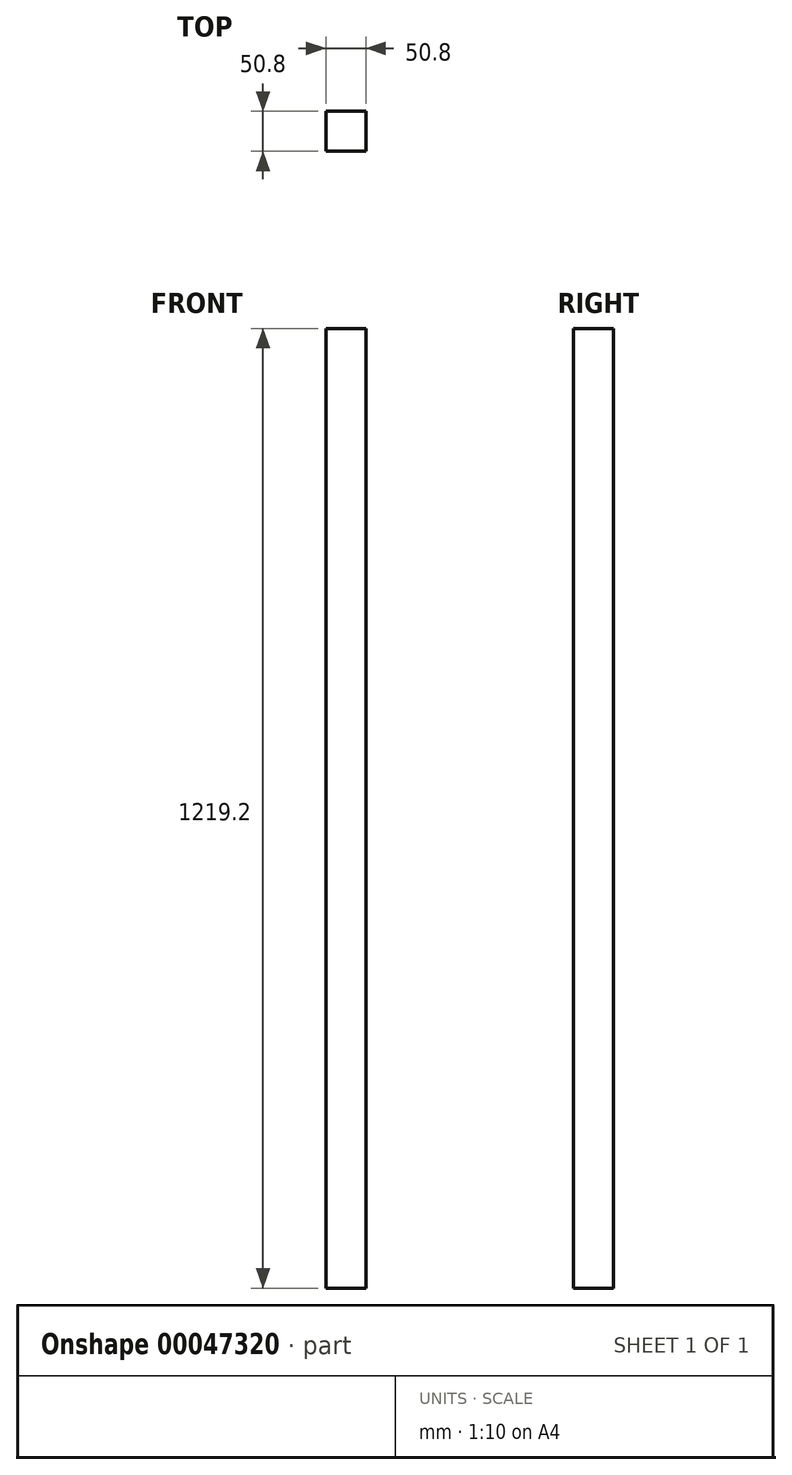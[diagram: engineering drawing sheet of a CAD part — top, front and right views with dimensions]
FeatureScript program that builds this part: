
annotation { "Feature Type Name" : "Feature", "Feature Type Description" : "" }
export const myFeature = defineFeature(function(context is Context, id is Id, definition is map)
    precondition{}
    {
        {
            var Q0;
            Q0=qCreatedBy(makeId("Top.planeOp"),FACE);
            var sketch = newSketch(context, id + "F0", { "sketchPlane" : qUnion([Q0])});
            skLineSegment(sketch, "E0.bottom", {"start": v(-76.33, 69.74) * mm, "end": v(-25.53, 69.74) * mm});
            skLineSegment(sketch, "E0.top", {"start": v(-76.33, 18.94) * mm, "end": v(-25.53, 18.94) * mm});
            skLineSegment(sketch, "E0.left", {"start": v(-76.33, 69.74) * mm, "end": v(-76.33, 18.94) * mm});
            skLineSegment(sketch, "E0.right", {"start": v(-25.53, 69.74) * mm, "end": v(-25.53, 18.94) * mm});
            skSolve(sketch);
        }
        {
            var Q0;
            Q0=makeQuery(id+"F0.imprint","IMPRINT",FACE,{"disambiguationData":[TD([[makeQuery(id+"F0.imprint","IMPRINT",EDGE,{"derivedFrom":sQuery(id+"F0.wireOp",EDGE,"E0.bottom")}),-1.0]])]});
            extrude(context, id + "F1", {"entities" : qUnion([Q0]), "depth" : 1219.2 * mm});
        }
    });
